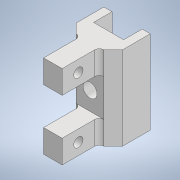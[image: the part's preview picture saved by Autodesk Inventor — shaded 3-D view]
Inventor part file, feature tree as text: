
AUTODESK INVENTOR PART (.ipt)
format: ipt  version: 2020 (Build 240168000, 168)  size: 240,640 bytes
history: native  units: mm
features: extrude x9, sketch x9, projected_geometry x9, reference x3, other x3, chamfer x1, fillet x1
ambient origin geometry x8: Origin, YZ Plane, XZ Plane, XY Plane, X Axis, Y Axis, Z Axis, Center Point
bodies: Solid1 (feature_tree)
feature tree (35):
  extrude  "Extrusion1"  Depth=10.0mm
  extrude  "Extrusion2"  Depth=3.0mm
  extrude  "Extrusion3"  Depth=1.75mm
  extrude  "Extrusion4"  Depth=1.75mm
  extrude  "Extrusion5"  Depth=4.0mm TaperAngle=0.0deg
  extrude  "Extrusion6"  Depth=5.0mm
  extrude  "Extrusion7"  Depth=5.0mm
  extrude  "Extrusion8"  Depth=8.0mm TaperAngle=0.0deg
  extrude  "Extrusion9"  Depth=3.0mm TaperAngle=0.0deg
  chamfer  "Chamfer1"  Distance=3.0mm
  fillet  "Fillet1"  Radius=3.5mm
  sketch  "Sketch1"  dims[d0=8.0mm d1=10.0mm]
  reference  "Reference1"
  sketch  "Sketch2"  dims[d2=4.0mm d3=0.0mm d4=3.0mm]
  projected_geometry  "Projected Loop1"
  sketch  "Sketch3"  dims[d5=4.0mm d6=0.0mm d7=1.75mm]
  projected_geometry  "Projected Loop2"
  reference  "Reference2"
  reference  "Reference3"
  sketch  "Sketch4"  dims[d8=8.0mm d9=1.75mm]
  projected_geometry  "Projected Loop3"
  sketch  "Sketch5"  dims[d10=8.0mm d11=4.0mm d12=0.0mm]
  projected_geometry  "Projected Loop4"
  sketch  "Sketch6"  dims[d13=10.0mm d14=5.0mm]
  projected_geometry  "Projected Loop5"
  sketch  "Sketch7"  dims[d15=10.0mm d16=5.0mm]
  projected_geometry  "Projected Loop6"
  sketch  "Sketch8"  dims[d17=8.0mm d18=0.0mm d19=8.0mm d20=0.0mm]
  projected_geometry  "Projected Loop7"
  sketch  "Sketch9"  dims[d21=8.0mm d22=0.0mm d23=3.0mm d24=0.0mm d25=3.0mm d26=0.0mm d27=3.5mm d28=2.0mm d29=3.5mm d30=2.0mm d31=4.0mm d32=0.0mm d33=2.0mm d34=2.0mm d35=45.0deg d36=1.0mm]
  projected_geometry  "Projected Loop8"
  projected_geometry  "Projected Loop9"
  parser-record x1  (decoder bookkeeping rows leaked as tree rows — omitted from the tree; the rows remain in map.json)
  other  "eye_bearing.iam"
  other  "eye_bearing_2:1"
note: 1 file-system path scrubbed to <path> (originals preserved in map.json)
